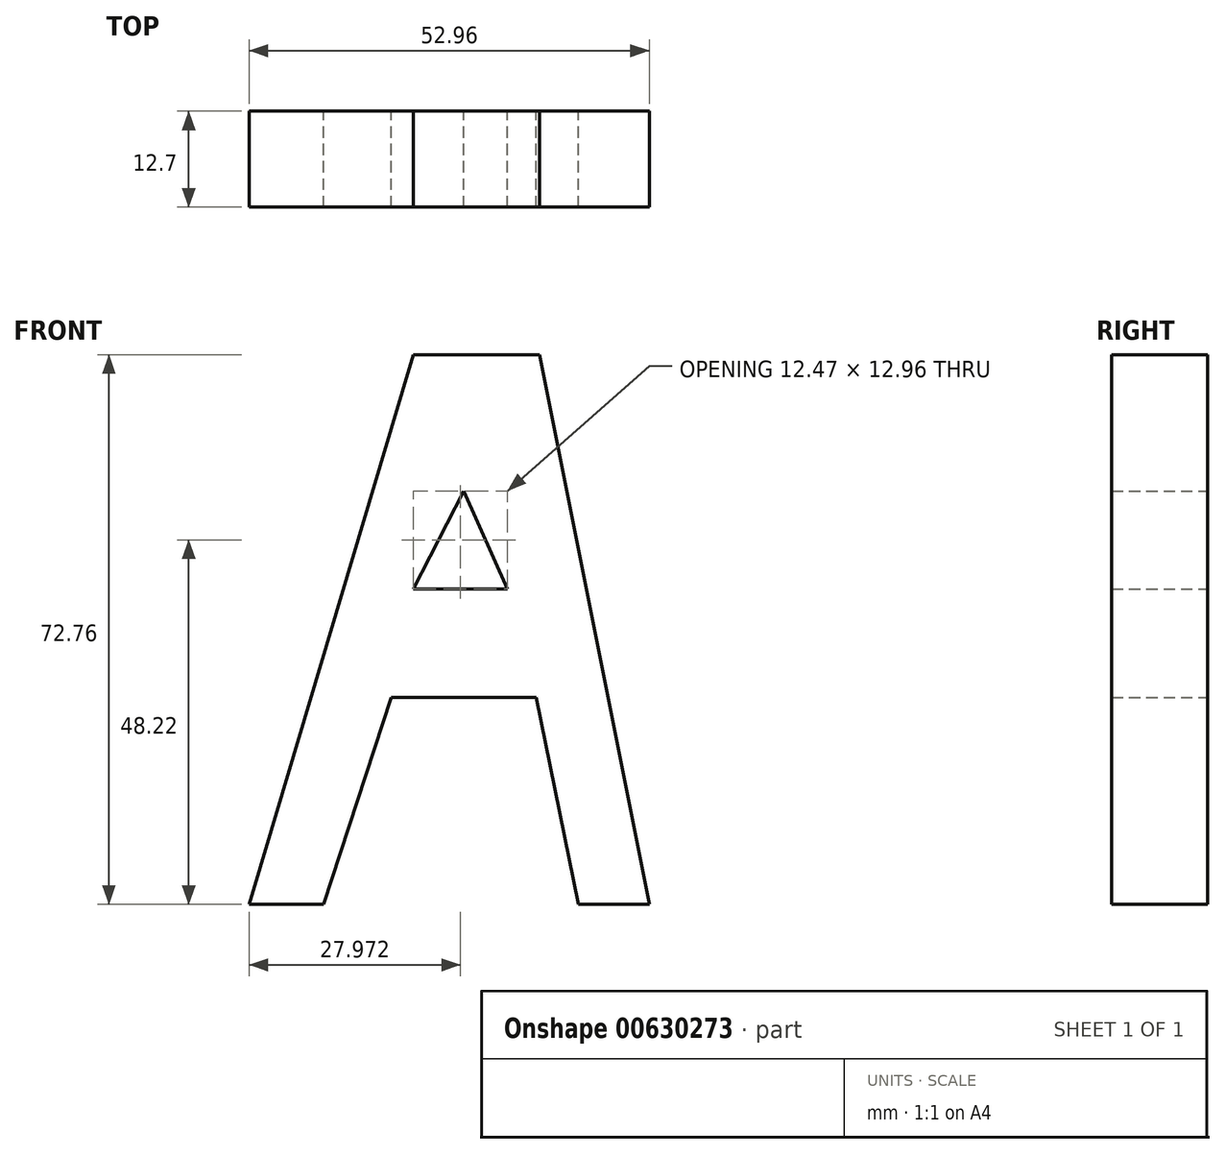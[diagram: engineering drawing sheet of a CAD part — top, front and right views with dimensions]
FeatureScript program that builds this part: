
annotation { "Feature Type Name" : "Feature", "Feature Type Description" : "" }
export const myFeature = defineFeature(function(context is Context, id is Id, definition is map)
    precondition{}
    {
        {
            var Q0;
            Q0=qCreatedBy(makeId("Front.planeOp"),FACE);
            var sketch = newSketch(context, id + "F0", { "sketchPlane" : qUnion([Q0])});
            skLineSegment(sketch, "E0", {"start": v(-132.17, -27.4) * mm, "end": v(-110.43, 45.37) * mm});
            skLineSegment(sketch, "E1", {"start": v(-110.43, 45.37) * mm, "end": v(-93.76, 45.37) * mm});
            skLineSegment(sketch, "E2", {"start": v(-93.76, 45.37) * mm, "end": v(-79.2, -27.4) * mm});
            skLineSegment(sketch, "E3", {"start": v(-79.2, -27.4) * mm, "end": v(-88.57, -27.4) * mm});
            skLineSegment(sketch, "E4", {"start": v(-88.57, -27.4) * mm, "end": v(-94.16, 0) * mm});
            skLineSegment(sketch, "E5", {"start": v(-94.16, 0) * mm, "end": v(-113.37, 0) * mm});
            skLineSegment(sketch, "E6", {"start": v(-113.37, 0) * mm, "end": v(-122.32, -27.4) * mm});
            skLineSegment(sketch, "E7", {"start": v(-122.32, -27.4) * mm, "end": v(-132.17, -27.4) * mm});
            skLineSegment(sketch, "E8", {"start": v(-103.76, 27.31) * mm, "end": v(-110.43, 14.35) * mm});
            skPoint(sketch, "E8.startSnap0", {"position": v(-103.76, 0) * mm});
            skLineSegment(sketch, "E9", {"start": v(-110.43, 14.35) * mm, "end": v(-97.97, 14.35) * mm});
            skLineSegment(sketch, "E10", {"start": v(-97.97, 14.35) * mm, "end": v(-103.76, 27.31) * mm});
            skSolve(sketch);
        }
        {
            var Q0;
            Q0=makeQuery(id+"F0.imprint","IMPRINT",FACE,{"disambiguationData":[TD([[makeQuery(id+"F0.imprint","IMPRINT",EDGE,{"derivedFrom":sQuery(id+"F0.wireOp",EDGE,"E0")}),-1.0]])]});
            extrude(context, id + "F1", {"entities" : qUnion([Q0]), "depth" : 12.7 * mm, "offsetDistance" : 25.4 * mm});
        }
    });
